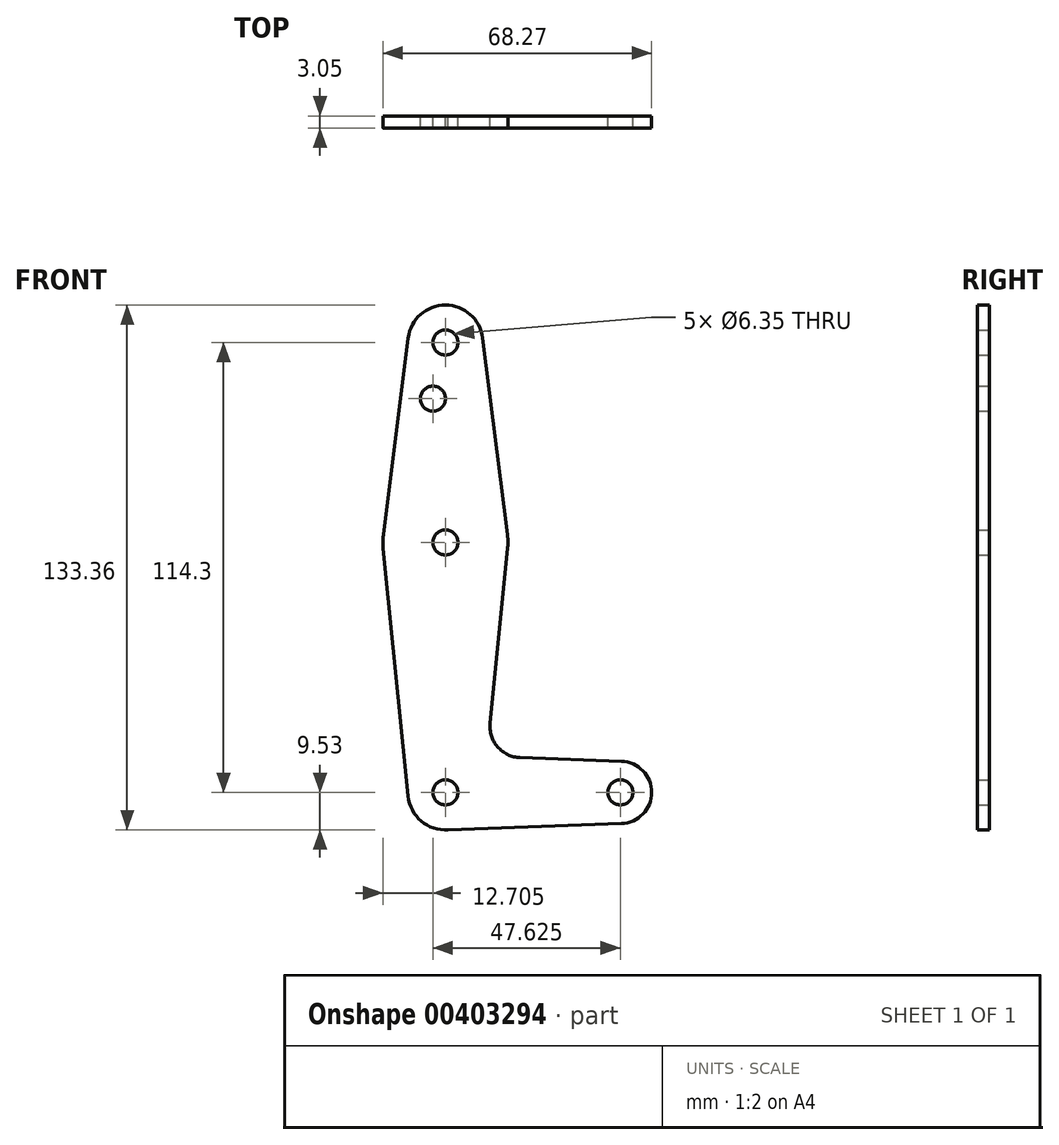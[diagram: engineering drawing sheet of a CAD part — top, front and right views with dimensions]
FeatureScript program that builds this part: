
annotation { "Feature Type Name" : "Feature", "Feature Type Description" : "" }
export const myFeature = defineFeature(function(context is Context, id is Id, definition is map)
    precondition{}
    {
        {
            var Q0;
            Q0=qCreatedBy(makeId("Front.planeOp"),FACE);
            var sketch = newSketch(context, id + "F0", { "sketchPlane" : qUnion([Q0])});
            skLineSegment(sketch, "E0", {"start": v(0, 114.3) * mm, "end": v(0, 0) * mm, "construction": true});
            skLineSegment(sketch, "E1", {"start": v(0, 0) * mm, "end": v(44.45, 0) * mm, "construction": true});
            skCircle(sketch, "E2", {"center": v(0, 114.3) * mm, "radius": 9.53 * mm});
            skCircle(sketch, "E3", {"center": v(0, 63.5) * mm, "radius": 15.88 * mm});
            skCircle(sketch, "E4", {"center": v(0, 0) * mm, "radius": 9.53 * mm});
            skCircle(sketch, "E5", {"center": v(44.45, 0) * mm, "radius": 7.94 * mm});
            skLineSegment(sketch, "E6", {"start": v(-9.45, 115.5) * mm, "end": v(-15.75, 65.48) * mm});
            skLineSegment(sketch, "E7", {"start": v(9.45, 115.5) * mm, "end": v(15.75, 65.48) * mm});
            skLineSegment(sketch, "E8", {"start": v(-15.8, 61.91) * mm, "end": v(-9.48, -0.95) * mm});
            skLineSegment(sketch, "E9", {"start": v(15.8, 61.91) * mm, "end": v(11.34, 17.59) * mm});
            skLineSegment(sketch, "E10", {"start": v(0, -9.53) * mm, "end": v(44.73, -7.93) * mm});
            skLineSegment(sketch, "E11", {"start": v(18.97, 8.85) * mm, "end": v(44.73, 7.93) * mm});
            skCircle(sketch, "E12", {"center": v(0, 114.3) * mm, "radius": 3.18 * mm});
            skCircle(sketch, "E13", {"center": v(-3.17, 100.03) * mm, "radius": 3.18 * mm});
            skCircle(sketch, "E14", {"center": v(0, 63.5) * mm, "radius": 3.18 * mm});
            skCircle(sketch, "E15", {"center": v(0, 0) * mm, "radius": 3.18 * mm});
            skCircle(sketch, "E16", {"center": v(44.45, 0) * mm, "radius": 3.18 * mm});
            skPoint(sketch, "E17.newPointB", {"position": v(0, 9.53) * mm});
            skArc(sketch, "E17.filletArc", {"start": v(11.34, 17.59) * mm, "mid": v(13.26, 11.57) * mm, "end": v(18.97, 8.85) * mm});
            skSolve(sketch);
        }
        {
            var Q0;
            Q0 = qSketchRegion(id + "F0", true);
            extrude(context, id + "F1", {"entities" : qUnion([Q0]), "depth" : 3.05 * mm});
        }
    });
